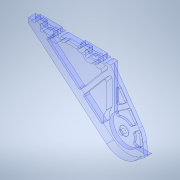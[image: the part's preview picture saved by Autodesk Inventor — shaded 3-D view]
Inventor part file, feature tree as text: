
AUTODESK INVENTOR PART (.ipt)
format: ipt  version: 2020.2 (Build 242310000, 310)  size: 858,112 bytes
history: native  units: mm
features: sketch x18, extrude x18, projected_geometry x14, other x3, fillet x2
ambient origin geometry x8: Origin, YZ Plane, XZ Plane, XY Plane, X Axis, Y Axis, Z Axis, Center Point
bodies: Body1 (feature_tree)
feature tree (55):
  other  "ソリッド1"
  sketch  "スケッチ1"
  extrude  "押し出し1"  Depth=5.0mm
  extrude  "押し出し2"  Depth=3.0mm
  extrude  "押し出し3"  Depth=5.0mm
  extrude  "押し出し4"  Depth=3.0mm
  sketch  "スケッチ4"
  extrude  "押し出し5"  Depth=3.0mm
  extrude  "押し出し6"  Depth=5.0mm
  extrude  "押し出し7"  Depth=1.0mm
  sketch  "スケッチ6"
  extrude  "押し出し8"  Depth=5.0mm
  extrude  "押し出し9"  Depth=5.0mm
  sketch  "スケッチ8"
  extrude  "押し出し10"  Depth=2.0mm
  extrude  "押し出し11"  Depth=2.0mm
  extrude  "押し出し12"  Depth=2.0mm
  extrude  "押し出し13"  Depth=2.0mm
  sketch  "スケッチ9"
  extrude  "押し出し14"  Depth=2.0mm
  extrude  "押し出し15"  Depth=2.0mm
  sketch  "スケッチ10"
  sketch  "スケッチ11"
  sketch  "スケッチ12"
  sketch  "スケッチ13"
  sketch  "スケッチ14"
  extrude  "押し出し17"  Depth=2.0mm
  extrude  "押し出し18"  Depth=2.0mm
  fillet  "フィレット3"  Radius=2.0mm
  extrude  "押し出し19"  Depth=2.0mm
  fillet  "フィレット4"  Radius=2.0mm
  sketch  "スケッチ18"
  sketch  "スケッチ2"
  projected_geometry  "投影ループ1"
  sketch  "スケッチ3"
  projected_geometry  "投影ループ2"
  projected_geometry  "投影ループ3"
  sketch  "スケッチ5"
  projected_geometry  "投影ループ4"
  projected_geometry  "投影ループ5"
  projected_geometry  "投影ループ6"
  sketch  "スケッチ7"
  projected_geometry  "投影ループ7"
  projected_geometry  "投影ループ8"
  projected_geometry  "投影ループ9"
  projected_geometry  "投影ループ10"
  projected_geometry  "投影ループ11"
  projected_geometry  "投影ループ12"
  projected_geometry  "投影ループ13"
  sketch  "スケッチ15"
  sketch  "スケッチ16"
  sketch  "スケッチ17"
  projected_geometry  "投影ループ14"
  other  "断面エッジを投影1"
  other  "断面エッジを投影2"
